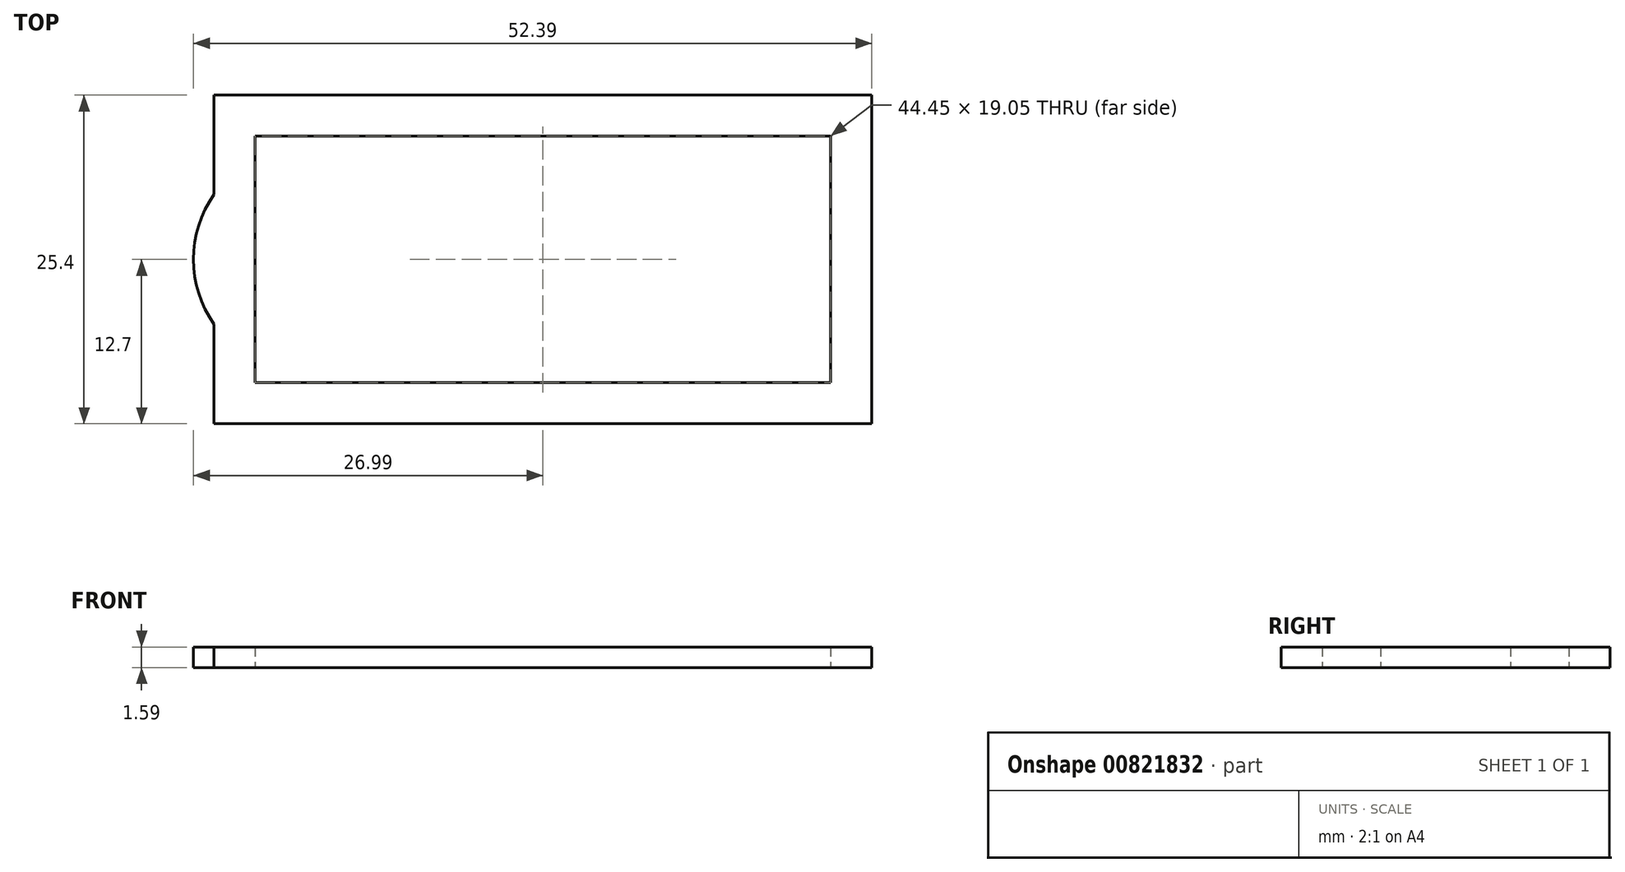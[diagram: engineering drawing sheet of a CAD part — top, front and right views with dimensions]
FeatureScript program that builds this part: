
annotation { "Feature Type Name" : "Feature", "Feature Type Description" : "" }
export const myFeature = defineFeature(function(context is Context, id is Id, definition is map)
    precondition{}
    {
        {
            var Q0;
            Q0=qCreatedBy(makeId("Top.planeOp"),FACE);
            var sketch = newSketch(context, id + "F0", { "sketchPlane" : qUnion([Q0])});
            skLineSegment(sketch, "E0.bottom", {"start": v(0, 0) * mm, "end": v(50.8, 0) * mm});
            skLineSegment(sketch, "E0.top", {"start": v(0, 25.4) * mm, "end": v(50.8, 25.4) * mm});
            skLineSegment(sketch, "E0.left", {"start": v(0, 0) * mm, "end": v(0, 25.4) * mm});
            skLineSegment(sketch, "E0.right", {"start": v(50.8, 0) * mm, "end": v(50.8, 25.4) * mm});
            skCircle(sketch, "E1", {"center": v(7.14, 12.7) * mm, "radius": 2.38 * mm});
            skPoint(sketch, "E1.centerSnap0", {"position": v(0, 12.7) * mm});
            skCircle(sketch, "E2.0", {"center": v(7.14, 12.7) * mm, "radius": 8.73 * mm});
            skLineSegment(sketch, "E3.0", {"start": v(3.18, 22.23) * mm, "end": v(47.62, 22.23) * mm});
            skLineSegment(sketch, "E3.1", {"start": v(3.18, 3.18) * mm, "end": v(3.18, 22.22) * mm});
            skLineSegment(sketch, "E3.2", {"start": v(3.18, 3.18) * mm, "end": v(47.62, 3.18) * mm});
            skLineSegment(sketch, "E3.3", {"start": v(47.62, 3.18) * mm, "end": v(47.62, 22.23) * mm});
            skSolve(sketch);
        }
        {
            var Q0;
            Q0 = qSketchRegion(id + "F0", true);
            extrude(context, id + "F1", {"entities" : qUnion([Q0]), "depth" : 1.59 * mm, "offsetDistance" : 25.4 * mm});
        }
    });
